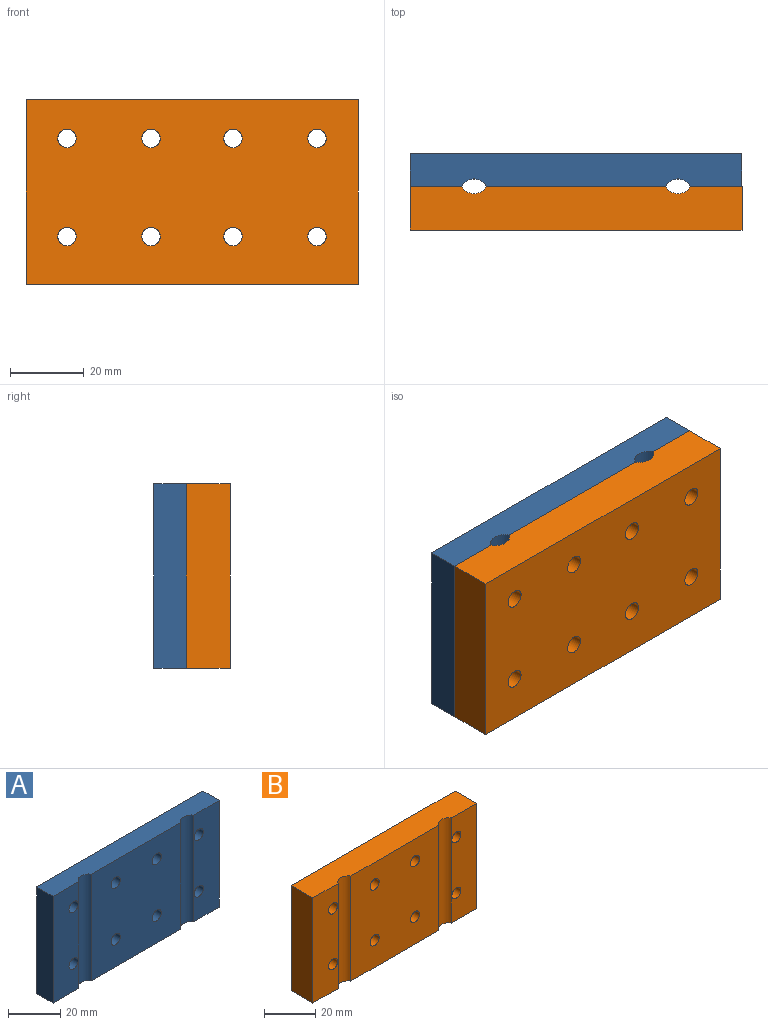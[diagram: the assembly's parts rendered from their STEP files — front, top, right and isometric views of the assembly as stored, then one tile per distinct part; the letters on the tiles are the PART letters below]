
ASSEMBLY  parts=2 mates=1
PART A: 74 faces, bbox 90x8.9x50 mm
  f0: cylinder r=2.5mm len=5mm, axis (0,-1,0), area 76.2mm2, adj f10,f67
  f1: cylinder r=2.5mm len=5mm, axis (0,-1,0), area 76.2mm2, adj f15,f66
  f2: cylinder r=2.5mm len=5mm, axis (0,-1,0), area 76.2mm2, adj f8,f59
  f3: cylinder r=2.5mm len=5mm, axis (0,-1,0), area 76.2mm2, adj f8,f52
  f4: cylinder r=2.5mm len=5mm, axis (0,-1,0), area 76.2mm2, adj f15,f45
  f5: cylinder r=2.5mm len=5mm, axis (0,-1,0), area 76.2mm2, adj f10,f32
  f6: cylinder r=2.5mm len=5mm, axis (0,-1,0), area 76.2mm2, adj f8,f25
  f7: cylinder r=2.5mm len=5mm, axis (0,-1,0), area 76.2mm2, adj f8,f18
  f8: plane 50x48.33mm, normal (0,-1,0), area 2338mm2, adj f2,f3,f6,f7,f11,f12,f16,f17
  f9: plane 90x50mm, normal (0,1,0), area 4061mm2, adj f11,f12,f13,f14,f19,f20,f21,f22
  f10: plane 50x13.84mm, normal (0,-1,0), area 652.5mm2, adj f0,f5,f11,f12,f13,f17
  f11: plane 90x8.85mm, normal (0,0,1), area 776.7mm2, adj f8,f9,f10,f13,f14,f15,f16,f17
  f12: plane 90x8.85mm, normal (0,0,-1), area 776.7mm2, adj f8,f9,f10,f13,f14,f15,f16,f17
  f13: plane 50x8.85mm, normal (-1,0,0), area 442.5mm2, adj f9,f10,f11,f12
  f14: plane 50x8.85mm, normal (1,0,0), area 442.5mm2, adj f9,f11,f12,f15
  f15: plane 50x13.84mm, normal (0,-1,0), area 652.5mm2, adj f1,f4,f11,f12,f14,f16
  f16: cylinder r=4.06mm len=50mm, axis (0,0,1), area 421.8mm2, adj f8,f11,f12,f15
  f17: cylinder r=4.06mm len=50mm, axis (0,0,1), area 421.8mm2, adj f8,f10,f11,f12
  f18: plane 9.19x7.96mm, normal (0,1,0), area 35.2mm2, adj f7,f19,f20,f21,f22,f23,f24
  f19: plane 4x3.98mm, normal (0.5,0,0.87), area 18.4mm2, adj f9,f18,f20,f24
  f20: plane 4.6x4mm, normal (1,0,0), area 18.4mm2, adj f9,f18,f19,f21
  f21: plane 4x3.98mm, normal (0.5,0,-0.87), area 18.4mm2, adj f9,f18,f20,f22
  f22: plane 4x3.98mm, normal (-0.5,0,-0.87), area 18.4mm2, adj f9,f18,f21,f23
  f23: plane 4.6x4mm, normal (-1,0,0), area 18.4mm2, adj f9,f18,f22,f24
  f24: plane 4x3.98mm, normal (-0.5,0,0.87), area 18.4mm2, adj f9,f18,f19,f23
  f25: plane 9.19x7.96mm, normal (0,1,0), area 35.2mm2, adj f6,f26,f27,f28,f29,f30,f31
  f26: plane 4x3.98mm, normal (0.5,0,0.87), area 18.4mm2, adj f9,f25,f27,f31
  f27: plane 4.6x4mm, normal (1,0,0), area 18.4mm2, adj f9,f25,f26,f28
  f28: plane 4x3.98mm, normal (0.5,0,-0.87), area 18.4mm2, adj f9,f25,f27,f29
  f29: plane 4x3.98mm, normal (-0.5,0,-0.87), area 18.4mm2, adj f9,f25,f28,f30
  f30: plane 4.6x4mm, normal (-1,0,0), area 18.4mm2, adj f9,f25,f29,f31
  f31: plane 4x3.98mm, normal (-0.5,0,0.87), area 18.4mm2, adj f9,f25,f26,f30
  f32: plane 9.19x7.96mm, normal (0,1,0), area 35.2mm2, adj f5,f33,f34,f35,f36,f37,f38
  f33: plane 4x3.98mm, normal (0.5,0,0.87), area 18.4mm2, adj f9,f32,f34,f38
  f34: plane 4.6x4mm, normal (1,0,0), area 18.4mm2, adj f9,f32,f33,f35
  f35: plane 4x3.98mm, normal (0.5,0,-0.87), area 18.4mm2, adj f9,f32,f34,f36
  f36: plane 4x3.98mm, normal (-0.5,0,-0.87), area 18.4mm2, adj f9,f32,f35,f37
  f37: plane 4.6x4mm, normal (-1,0,0), area 18.4mm2, adj f9,f32,f36,f38
  f38: plane 4x3.98mm, normal (-0.5,0,0.87), area 18.4mm2, adj f9,f32,f33,f37
  f39: plane 4x3.98mm, normal (0.5,0,0.87), area 18.4mm2, adj f9,f40,f44,f45
  f40: plane 4.6x4mm, normal (1,0,0), area 18.4mm2, adj f9,f39,f41,f45
  f41: plane 4x3.98mm, normal (0.5,0,-0.87), area 18.4mm2, adj f9,f40,f42,f45
  f42: plane 4x3.98mm, normal (-0.5,0,-0.87), area 18.4mm2, adj f9,f41,f43,f45
  f43: plane 4.6x4mm, normal (-1,0,0), area 18.4mm2, adj f9,f42,f44,f45
  f44: plane 4x3.98mm, normal (-0.5,0,0.87), area 18.4mm2, adj f9,f39,f43,f45
  f45: plane 9.19x7.96mm, normal (0,1,0), area 35.2mm2, adj f4,f39,f40,f41,f42,f43,f44
  f46: plane 4x3.98mm, normal (0.5,0,0.87), area 18.4mm2, adj f9,f47,f51,f52
  f47: plane 4.6x4mm, normal (1,0,0), area 18.4mm2, adj f9,f46,f48,f52
  f48: plane 4x3.98mm, normal (0.5,0,-0.87), area 18.4mm2, adj f9,f47,f49,f52
  f49: plane 4x3.98mm, normal (-0.5,0,-0.87), area 18.4mm2, adj f9,f48,f50,f52
  f50: plane 4.6x4mm, normal (-1,0,0), area 18.4mm2, adj f9,f49,f51,f52
  f51: plane 4x3.98mm, normal (-0.5,0,0.87), area 18.4mm2, adj f9,f46,f50,f52
  f52: plane 9.19x7.96mm, normal (0,1,0), area 35.2mm2, adj f3,f46,f47,f48,f49,f50,f51
  f53: plane 4x3.98mm, normal (0.5,0,0.87), area 18.4mm2, adj f9,f54,f58,f59
  f54: plane 4.6x4mm, normal (1,0,0), area 18.4mm2, adj f9,f53,f55,f59
  f55: plane 4x3.98mm, normal (0.5,0,-0.87), area 18.4mm2, adj f9,f54,f56,f59
  f56: plane 4x3.98mm, normal (-0.5,0,-0.87), area 18.4mm2, adj f9,f55,f57,f59
  f57: plane 4.6x4mm, normal (-1,0,0), area 18.4mm2, adj f9,f56,f58,f59
  f58: plane 4x3.98mm, normal (-0.5,0,0.87), area 18.4mm2, adj f9,f53,f57,f59
  f59: plane 9.19x7.96mm, normal (0,1,0), area 35.2mm2, adj f2,f53,f54,f55,f56,f57,f58
  f60: plane 4x3.98mm, normal (0.5,0,0.87), area 18.4mm2, adj f9,f61,f65,f66
  f61: plane 4.6x4mm, normal (1,0,0), area 18.4mm2, adj f9,f60,f62,f66
  f62: plane 4x3.98mm, normal (0.5,0,-0.87), area 18.4mm2, adj f9,f61,f63,f66
  f63: plane 4x3.98mm, normal (-0.5,0,-0.87), area 18.4mm2, adj f9,f62,f64,f66
  f64: plane 4.6x4mm, normal (-1,0,0), area 18.4mm2, adj f9,f63,f65,f66
  f65: plane 4x3.98mm, normal (-0.5,0,0.87), area 18.4mm2, adj f9,f60,f64,f66
  f66: plane 9.19x7.96mm, normal (0,1,0), area 35.2mm2, adj f1,f60,f61,f62,f63,f64,f65
  f67: plane 9.19x7.96mm, normal (0,1,0), area 35.2mm2, adj f0,f68,f69,f70,f71,f72,f73
  f68: plane 4x3.98mm, normal (0.5,0,0.87), area 18.4mm2, adj f9,f67,f69,f73
  f69: plane 4.6x4mm, normal (1,0,0), area 18.4mm2, adj f9,f67,f68,f70
  f70: plane 4x3.98mm, normal (0.5,0,-0.87), area 18.4mm2, adj f9,f67,f69,f71
  f71: plane 4x3.98mm, normal (-0.5,0,-0.87), area 18.4mm2, adj f9,f67,f70,f72
  f72: plane 4.6x4mm, normal (-1,0,0), area 18.4mm2, adj f9,f67,f71,f73
  f73: plane 4x3.98mm, normal (-0.5,0,0.87), area 18.4mm2, adj f9,f67,f68,f72
PART B: 18 faces, bbox 90x11.9x50 mm
  f0: plane 50x48.33mm, normal (0,-1,0), area 2338mm2, adj f3,f4,f8,f9,f12,f13,f16,f17
  f1: plane 90x50mm, normal (0,1,0), area 4342.9mm2, adj f3,f4,f5,f6,f10,f11,f12,f13
  f2: plane 50x13.84mm, normal (0,-1,0), area 652.5mm2, adj f3,f4,f5,f9,f10,f15
  f3: plane 90x11.85mm, normal (0,0,1), area 1046.7mm2, adj f0,f1,f2,f5,f6,f7,f8,f9
  f4: plane 90x11.85mm, normal (0,0,-1), area 1046.7mm2, adj f0,f1,f2,f5,f6,f7,f8,f9
  f5: plane 50x11.85mm, normal (-1,0,0), area 592.5mm2, adj f1,f2,f3,f4
  f6: plane 50x11.85mm, normal (1,0,0), area 592.5mm2, adj f1,f3,f4,f7
  f7: plane 50x13.84mm, normal (0,-1,0), area 652.5mm2, adj f3,f4,f6,f8,f11,f14
  f8: cylinder r=4.06mm len=50mm, axis (0,0,1), area 421.8mm2, adj f0,f3,f4,f7
  f9: cylinder r=4.06mm len=50mm, axis (0,0,1), area 421.8mm2, adj f0,f2,f3,f4
  f10: cylinder r=2.5mm len=11.85mm, axis (0,-1,0), area 186.1mm2, adj f1,f2
  f11: cylinder r=2.5mm len=11.85mm, axis (0,-1,0), area 186.1mm2, adj f1,f7
  f12: cylinder r=2.5mm len=11.85mm, axis (0,-1,0), area 186.1mm2, adj f0,f1
  f13: cylinder r=2.5mm len=11.85mm, axis (0,-1,0), area 186.1mm2, adj f0,f1
  f14: cylinder r=2.5mm len=11.85mm, axis (0,-1,0), area 186.1mm2, adj f1,f7
  f15: cylinder r=2.5mm len=11.85mm, axis (0,-1,0), area 186.1mm2, adj f1,f2
  f16: cylinder r=2.5mm len=11.85mm, axis (0,-1,0), area 186.1mm2, adj f0,f1
  f17: cylinder r=2.5mm len=11.85mm, axis (0,-1,0), area 186.1mm2, adj f0,f1
PLACE A t=(143.85,134.11,66.16)mm
PLACE B rot(axis=(0,0,1),180deg) t=(139.91,110.41,66.16)mm
MATE fastened B.f5 <-> A.f14  axis (1,0,0) through (186.88,122.26,94.41)mm
